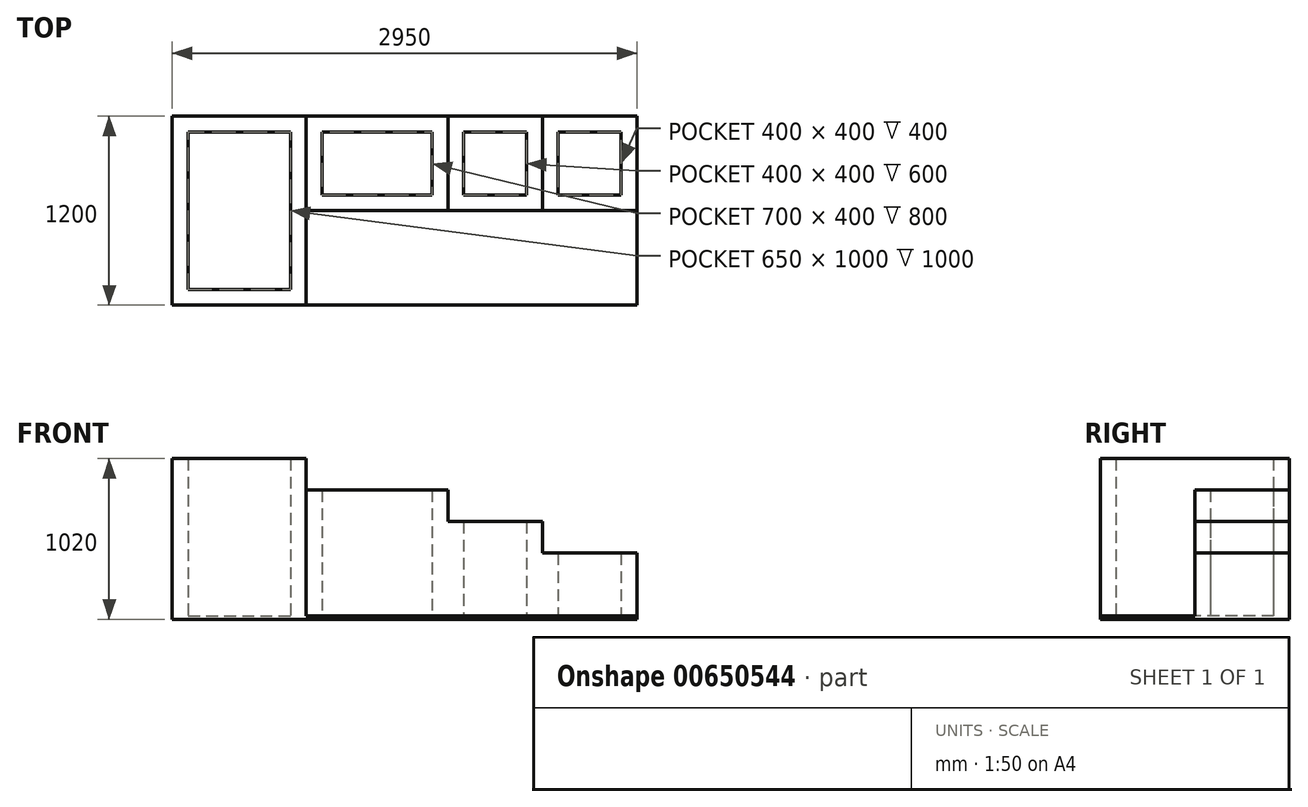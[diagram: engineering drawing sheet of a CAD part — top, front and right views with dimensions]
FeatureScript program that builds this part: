
annotation { "Feature Type Name" : "Feature", "Feature Type Description" : "" }
export const myFeature = defineFeature(function(context is Context, id is Id, definition is map)
    precondition{}
    {
        {
            var Q0;
            Q0=qCreatedBy(makeId("Top.planeOp"),FACE);
            var sketch = newSketch(context, id + "F0", { "sketchPlane" : qUnion([Q0])});
            skLineSegment(sketch, "E0.bottom", {"start": v(0, 0) * mm, "end": v(-2563.64, 0) * mm});
            skLineSegment(sketch, "E0.top", {"start": v(0, 1200) * mm, "end": v(-2950, 1200) * mm});
            skLineSegment(sketch, "E0.left", {"start": v(0, 0) * mm, "end": v(0, 1200) * mm});
            skLineSegment(sketch, "E0.right", {"start": v(-2950, 0) * mm, "end": v(-2950, 1200) * mm});
            skLineSegment(sketch, "E1", {"start": v(-2563.64, 0) * mm, "end": v(-2950, 0) * mm});
            skSolve(sketch);
        }
        {
            var Q0;
            Q0=makeQuery(id+"F0.imprint","IMPRINT",FACE,{"disambiguationData":[TD([[makeQuery(id+"F0.imprint","IMPRINT",EDGE,{"derivedFrom":sQuery(id+"F0.wireOp",EDGE,"E0.bottom")}),-1.0]])]});
            extrude(context, id + "F1", {"entities" : qUnion([Q0]), "depth" : 20 * mm, "offsetDistance" : 25 * mm});
        }
        {
            var Q0;
            Q0=makeQuery(id+"F1.opExtrude","CAP_FACE",FACE,{"disambiguationData":[OSD([sQuery(id+"F0.wireOp",EDGE,"E0.bottom"),sQuery(id+"F0.wireOp",EDGE,"E0.top"),sQuery(id+"F0.wireOp",EDGE,"E0.left"),sQuery(id+"F0.wireOp",EDGE,"E0.right"),sQuery(id+"F0.wireOp",EDGE,"EcOLhzoJ-yrHA-FEvU-6dDI-CAjuHtf4V0fh.bottom"),sQuery(id+"F0.wireOp",EDGE,"EcOLhzoJ-yrHA-FEvU-6dDI-CAjuHtf4V0fh.top"),sQuery(id+"F0.wireOp",EDGE,"EcOLhzoJ-yrHA-FEvU-6dDI-CAjuHtf4V0fh.left"),sQuery(id+"F0.wireOp",EDGE,"EcOLhzoJ-yrHA-FEvU-6dDI-CAjuHtf4V0fh.right")])],"isStart":false});
            var sketch = newSketch(context, id + "F2", { "sketchPlane" : qUnion([Q0])});
            skLineSegment(sketch, "E2.bottom", {"start": v(0, 1200) * mm, "end": v(-600, 1200) * mm});
            skLineSegment(sketch, "E2.top", {"start": v(0, 600) * mm, "end": v(-600, 600) * mm});
            skLineSegment(sketch, "E2.left", {"start": v(0, 1200) * mm, "end": v(0, 600) * mm});
            skLineSegment(sketch, "E2.right", {"start": v(-600, 1200) * mm, "end": v(-600, 600) * mm});
            skLineSegment(sketch, "E3.bottom", {"start": v(-500, 1100) * mm, "end": v(-100, 1100) * mm});
            skLineSegment(sketch, "E3.top", {"start": v(-500, 700) * mm, "end": v(-100, 700) * mm});
            skLineSegment(sketch, "E3.left", {"start": v(-500, 1100) * mm, "end": v(-500, 700) * mm});
            skLineSegment(sketch, "E3.right", {"start": v(-100, 1100) * mm, "end": v(-100, 700) * mm});
            skSolve(sketch);
        }
        {
            var Q0;
            Q0=qSketchRegion(id+"F2",true);
            extrude(context, id + "F3", {"entities" : qUnion([Q0]), "operationType" : NewBodyOperationType.ADD, "depth" : 400 * mm, "offsetDistance" : 25 * mm});
        }
        {
            var Q0;
            {var subQ0=sQuery(id+"F0.wireOp",EDGE,"E0.left");var subQ1=sQuery(id+"F0.wireOp",EDGE,"EcOLhzoJ-yrHA-FEvU-6dDI-CAjuHtf4V0fh.right");var subQ2=sQuery(id+"F0.wireOp",EDGE,"EcOLhzoJ-yrHA-FEvU-6dDI-CAjuHtf4V0fh.left");var subQ3=sQuery(id+"F0.wireOp",EDGE,"EcOLhzoJ-yrHA-FEvU-6dDI-CAjuHtf4V0fh.top");var subQ4=sQuery(id+"F0.wireOp",EDGE,"EcOLhzoJ-yrHA-FEvU-6dDI-CAjuHtf4V0fh.bottom");var subQ5=sQuery(id+"F0.wireOp",EDGE,"E0.bottom");var subQ6=sQuery(id+"F0.wireOp",EDGE,"E0.right");var subQ7=sQuery(id+"F0.wireOp",EDGE,"E0.top");Q0=makeQuery(id+"F3.boolean.opBoolean","SPLIT",FACE,{"disambiguationData":[TD([makeQuery(id+"F1.opExtrude","SWEPT_FACE",FACE,{"disambiguationData":[OSD([subQ5])]})])],"derivedFrom":makeQuery(id+"F1.opExtrude","CAP_FACE",FACE,{"disambiguationData":[OSD([subQ5,subQ7,subQ0,subQ6,subQ4,subQ3,subQ2,subQ1])],"isStart":false})});}
            var sketch = newSketch(context, id + "F4", { "sketchPlane" : qUnion([Q0])});
            skLineSegment(sketch, "E4.bottom", {"start": v(-600, 600) * mm, "end": v(-1200, 600) * mm});
            skLineSegment(sketch, "E4.top", {"start": v(-600, 1200) * mm, "end": v(-1200, 1200) * mm});
            skLineSegment(sketch, "E4.left", {"start": v(-600, 600) * mm, "end": v(-600, 1200) * mm});
            skLineSegment(sketch, "E4.right", {"start": v(-1200, 600) * mm, "end": v(-1200, 1200) * mm});
            skLineSegment(sketch, "E5.bottom", {"start": v(-700, 700) * mm, "end": v(-1100, 700) * mm});
            skLineSegment(sketch, "E5.top", {"start": v(-700, 1100) * mm, "end": v(-1100, 1100) * mm});
            skLineSegment(sketch, "E5.left", {"start": v(-700, 700) * mm, "end": v(-700, 1100) * mm});
            skLineSegment(sketch, "E5.right", {"start": v(-1100, 700) * mm, "end": v(-1100, 1100) * mm});
            skSolve(sketch);
        }
        {
            var Q0;
            Q0=qSketchRegion(id+"F4",true);
            extrude(context, id + "F5", {"entities" : qUnion([Q0]), "operationType" : NewBodyOperationType.ADD, "depth" : 600 * mm, "offsetDistance" : 25 * mm});
        }
        {
            var Q0;
            {var subQ1=sQuery(id+"F0.wireOp",EDGE,"E0.left");var subQ3=sQuery(id+"F0.wireOp",EDGE,"EcOLhzoJ-yrHA-FEvU-6dDI-CAjuHtf4V0fh.right");var subQ5=sQuery(id+"F0.wireOp",EDGE,"EcOLhzoJ-yrHA-FEvU-6dDI-CAjuHtf4V0fh.left");var subQ8=sQuery(id+"F0.wireOp",EDGE,"EcOLhzoJ-yrHA-FEvU-6dDI-CAjuHtf4V0fh.top");var subQ11=sQuery(id+"F0.wireOp",EDGE,"EcOLhzoJ-yrHA-FEvU-6dDI-CAjuHtf4V0fh.bottom");var subQ13=sQuery(id+"F0.wireOp",EDGE,"E0.bottom");var subQ14=makeQuery(id+"F1.opExtrude","SWEPT_FACE",FACE,{"disambiguationData":[OSD([subQ13])]});var subQ15=sQuery(id+"F0.wireOp",EDGE,"E0.right");var subQ17=sQuery(id+"F0.wireOp",EDGE,"E0.top");Q0=makeQuery(id+"F5.boolean.opBoolean","SPLIT",FACE,{"disambiguationData":[TD([subQ14])],"derivedFrom":makeQuery(id+"F3.boolean.opBoolean","SPLIT",FACE,{"disambiguationData":[TD([subQ14])],"derivedFrom":makeQuery(id+"F1.opExtrude","CAP_FACE",FACE,{"disambiguationData":[OSD([subQ13,subQ17,subQ1,subQ15,subQ11,subQ8,subQ5,subQ3])],"isStart":false})})});}
            var sketch = newSketch(context, id + "F6", { "sketchPlane" : qUnion([Q0])});
            skLineSegment(sketch, "E6.bottom", {"start": v(-1200, 600) * mm, "end": v(-2100, 600) * mm});
            skLineSegment(sketch, "E6.top", {"start": v(-1200, 1200) * mm, "end": v(-2100, 1200) * mm});
            skLineSegment(sketch, "E6.left", {"start": v(-1200, 600) * mm, "end": v(-1200, 1200) * mm});
            skLineSegment(sketch, "E6.right", {"start": v(-2100, 600) * mm, "end": v(-2100, 1200) * mm});
            skLineSegment(sketch, "E7.bottom", {"start": v(-1300, 700) * mm, "end": v(-2000, 700) * mm});
            skLineSegment(sketch, "E7.top", {"start": v(-1300, 1100) * mm, "end": v(-2000, 1100) * mm});
            skLineSegment(sketch, "E7.left", {"start": v(-1300, 700) * mm, "end": v(-1300, 1100) * mm});
            skLineSegment(sketch, "E7.right", {"start": v(-2000, 700) * mm, "end": v(-2000, 1100) * mm});
            skSolve(sketch);
        }
        {
            var Q0;
            Q0=qSketchRegion(id+"F6",true);
            extrude(context, id + "F7", {"entities" : qUnion([Q0]), "operationType" : NewBodyOperationType.ADD, "depth" : 800 * mm, "offsetDistance" : 25 * mm});
        }
        {
            var Q0;
            {var subQ1=sQuery(id+"F0.wireOp",EDGE,"E0.left");var subQ3=sQuery(id+"F0.wireOp",EDGE,"EcOLhzoJ-yrHA-FEvU-6dDI-CAjuHtf4V0fh.right");var subQ5=sQuery(id+"F0.wireOp",EDGE,"EcOLhzoJ-yrHA-FEvU-6dDI-CAjuHtf4V0fh.left");var subQ8=sQuery(id+"F0.wireOp",EDGE,"EcOLhzoJ-yrHA-FEvU-6dDI-CAjuHtf4V0fh.top");var subQ11=sQuery(id+"F0.wireOp",EDGE,"EcOLhzoJ-yrHA-FEvU-6dDI-CAjuHtf4V0fh.bottom");var subQ13=sQuery(id+"F0.wireOp",EDGE,"E0.bottom");var subQ14=makeQuery(id+"F1.opExtrude","SWEPT_FACE",FACE,{"disambiguationData":[OSD([subQ13])]});var subQ15=sQuery(id+"F0.wireOp",EDGE,"E0.right");var subQ17=sQuery(id+"F0.wireOp",EDGE,"E0.top");Q0=makeQuery(id+"F7.boolean.opBoolean","SPLIT",FACE,{"disambiguationData":[TD([subQ14])],"derivedFrom":makeQuery(id+"F5.boolean.opBoolean","SPLIT",FACE,{"disambiguationData":[TD([subQ14])],"derivedFrom":makeQuery(id+"F3.boolean.opBoolean","SPLIT",FACE,{"disambiguationData":[TD([subQ14])],"derivedFrom":makeQuery(id+"F1.opExtrude","CAP_FACE",FACE,{"disambiguationData":[OSD([subQ13,subQ17,subQ1,subQ15,subQ11,subQ8,subQ5,subQ3])],"isStart":false})})})});}
            var sketch = newSketch(context, id + "F8", { "sketchPlane" : qUnion([Q0])});
            skLineSegment(sketch, "E8.bottom", {"start": v(-2950, 1200) * mm, "end": v(-2100, 1200) * mm});
            skLineSegment(sketch, "E8.top", {"start": v(-2950, 0) * mm, "end": v(-2100, 0) * mm});
            skLineSegment(sketch, "E8.left", {"start": v(-2950, 1200) * mm, "end": v(-2950, 0) * mm});
            skLineSegment(sketch, "E8.right", {"start": v(-2100, 1200) * mm, "end": v(-2100, 0) * mm});
            skLineSegment(sketch, "E9.bottom", {"start": v(-2850, 1100) * mm, "end": v(-2200, 1100) * mm});
            skLineSegment(sketch, "E9.top", {"start": v(-2850, 100) * mm, "end": v(-2200, 100) * mm});
            skLineSegment(sketch, "E9.left", {"start": v(-2850, 1100) * mm, "end": v(-2850, 100) * mm});
            skLineSegment(sketch, "E9.right", {"start": v(-2200, 1100) * mm, "end": v(-2200, 100) * mm});
            skSolve(sketch);
        }
        {
            var Q0;
            Q0=qSketchRegion(id+"F8",true);
            extrude(context, id + "F9", {"entities" : qUnion([Q0]), "operationType" : NewBodyOperationType.ADD, "depth" : 1000 * mm, "offsetDistance" : 25 * mm});
        }
    });
